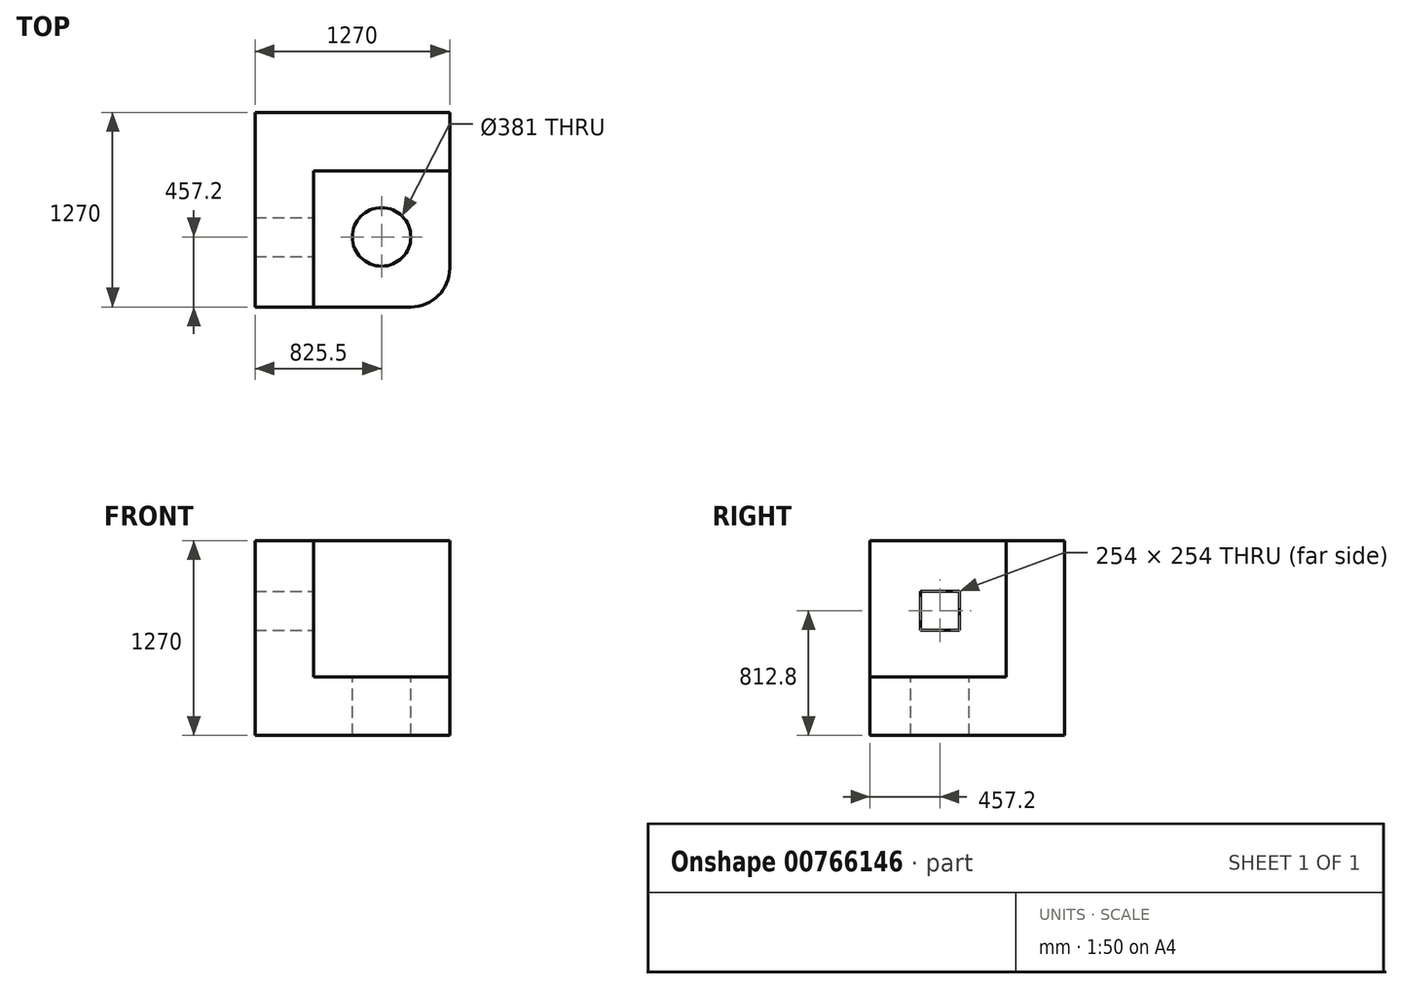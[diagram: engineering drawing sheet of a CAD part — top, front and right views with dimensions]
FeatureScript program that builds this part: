
annotation { "Feature Type Name" : "Feature", "Feature Type Description" : "" }
export const myFeature = defineFeature(function(context is Context, id is Id, definition is map)
    precondition{}
    {
        {
            var Q0;
            Q0=qCreatedBy(makeId("Front.planeOp"),FACE);
            var sketch = newSketch(context, id + "F0", { "sketchPlane" : qUnion([Q0])});
            skLineSegment(sketch, "E0.bottom", {"start": v(635, -635) * mm, "end": v(-635, -635) * mm});
            skLineSegment(sketch, "E0.top", {"start": v(635, 635) * mm, "end": v(-635, 635) * mm});
            skLineSegment(sketch, "E0.left", {"start": v(635, -635) * mm, "end": v(635, 635) * mm});
            skLineSegment(sketch, "E0.right", {"start": v(-635, -635) * mm, "end": v(-635, 635) * mm});
            skPoint(sketch, "E0.middle", {"position": v(0, 0) * mm});
            skSolve(sketch);
        }
        {
            var Q0;
            Q0 = qSketchRegion(id + "F0", true);
            extrude(context, id + "F1", {"entities" : qUnion([Q0]), "depth" : 1270 * mm, "offsetDistance" : 25.4 * mm});
        }
        {
            var Q0;
            Q0=makeQuery(id+"F1.opExtrude","CAP_FACE",FACE,{"disambiguationData":[OSD([sQuery(id+"F0.wireOp",EDGE,"E0.bottom"),sQuery(id+"F0.wireOp",EDGE,"E0.top"),sQuery(id+"F0.wireOp",EDGE,"E0.left"),sQuery(id+"F0.wireOp",EDGE,"E0.right")])],"isStart":false});
            var sketch = newSketch(context, id + "F2", { "sketchPlane" : qUnion([Q0])});
            skLineSegment(sketch, "E1", {"start": v(-635, 635) * mm, "end": v(-254, 635) * mm});
            skLineSegment(sketch, "E2", {"start": v(-254, 635) * mm, "end": v(-254, -254) * mm});
            skLineSegment(sketch, "E3", {"start": v(-254, -254) * mm, "end": v(635, -254) * mm});
            skSolve(sketch);
        }
        {
            var Q0;
            {var subQ0=sQuery(id+"F2.wireOp",EDGE,"E2");Q0=makeQuery(id+"F2.imprint","IMPRINT",FACE,{"disambiguationData":[TD([[makeQuery(id+"F2.imprint","IMPRINT",EDGE,{"derivedFrom":subQ0}),1.0]])]});}
            extrude(context, id + "F3", {"entities" : qUnion([Q0]), "operationType" : NewBodyOperationType.REMOVE, "oppositeDirection" : true, "depth" : 889 * mm, "offsetDistance" : 25.4 * mm});
        }
        {
            var Q0;
            Q0=makeQuery(id+"F3.boolean.opBoolean","COPY",FACE,{"derivedFrom":makeQuery(id+"F3.opExtrude","SWEPT_FACE",FACE,{"disambiguationData":[OSD([sQuery(id+"F2.wireOp",EDGE,"E2")])]})});
            var sketch = newSketch(context, id + "F4", { "sketchPlane" : qUnion([Q0])});
            skLineSegment(sketch, "E4", {"start": v(-1270, 635) * mm, "end": v(-939.8, 635) * mm});
            skLineSegment(sketch, "E5", {"start": v(-939.8, 635) * mm, "end": v(-939.8, 304.8) * mm});
            skLineSegment(sketch, "E6.bottom", {"start": v(-939.8, 304.8) * mm, "end": v(-685.8, 304.8) * mm});
            skLineSegment(sketch, "E6.top", {"start": v(-939.8, 50.8) * mm, "end": v(-685.8, 50.8) * mm});
            skLineSegment(sketch, "E6.left", {"start": v(-939.8, 304.8) * mm, "end": v(-939.8, 50.8) * mm});
            skLineSegment(sketch, "E6.right", {"start": v(-685.8, 304.8) * mm, "end": v(-685.8, 50.8) * mm});
            skSolve(sketch);
        }
        {
            var Q0;
            Q0=makeQuery(id+"F4.imprint","IMPRINT",FACE,{"disambiguationData":[TD([[makeQuery(id+"F4.imprint","IMPRINT",EDGE,{"derivedFrom":sQuery(id+"F4.wireOp",EDGE,"E6.bottom")}),-1.0]])]});
            extrude(context, id + "F5", {"entities" : qUnion([Q0]), "operationType" : NewBodyOperationType.ADD, "depth" : 381 * mm, "offsetDistance" : 25.4 * mm});
        }
        {
            var Q0;
            Q0=makeQuery(id+"F5.opExtrude","CAP_FACE",FACE,{"disambiguationData":[OSD([sQuery(id+"F4.wireOp",EDGE,"E6.bottom"),sQuery(id+"F4.wireOp",EDGE,"E6.top"),sQuery(id+"F4.wireOp",EDGE,"E6.left"),sQuery(id+"F4.wireOp",EDGE,"E6.right")])],"isStart":false});
            extrude(context, id + "F6", {"entities" : qUnion([Q0]), "operationType" : NewBodyOperationType.REMOVE, "oppositeDirection" : true, "depth" : 762 * mm, "offsetDistance" : 25.4 * mm});
        }
        {
            var Q0;
            Q0=makeQuery(id+"F3.boolean.opBoolean","COPY",FACE,{"derivedFrom":makeQuery(id+"F3.opExtrude","SWEPT_FACE",FACE,{"disambiguationData":[OSD([sQuery(id+"F2.wireOp",EDGE,"E3")])]})});
            var sketch = newSketch(context, id + "F7", { "sketchPlane" : qUnion([Q0])});
            skLineSegment(sketch, "E7", {"start": v(635, -1270) * mm, "end": v(190.5, -1270) * mm});
            skLineSegment(sketch, "E8", {"start": v(190.5, -1270) * mm, "end": v(190.5, -812.8) * mm});
            skCircle(sketch, "E9", {"center": v(190.5, -812.8) * mm, "radius": 190.5 * mm});
            skSolve(sketch);
        }
        {
            var Q0;
            Q0=makeQuery(id+"F7.imprint","IMPRINT",FACE,{"disambiguationData":[TD([[makeQuery(id+"F7.imprint","IMPRINT",EDGE,{"derivedFrom":sQuery(id+"F7.wireOp",EDGE,"E9")}),1.0]])]});
            extrude(context, id + "F8", {"entities" : qUnion([Q0]), "operationType" : NewBodyOperationType.REMOVE, "oppositeDirection" : true, "depth" : 381 * mm, "offsetDistance" : 25.4 * mm});
        }
        {
            var Q0;
            Q0=makeQuery(id+"F1.opExtrude","CAP_EDGE",EDGE,{"disambiguationData":[OSD([sQuery(id+"F0.wireOp",EDGE,"E0.left")])],"isStart":false});
            fillet(context, id + "F9", {"entities" : qUnion([Q0]), "radius" : 254 * mm, "tangentPropagation" : true, "allowEdgeOverflow" : false});
        }
    });
